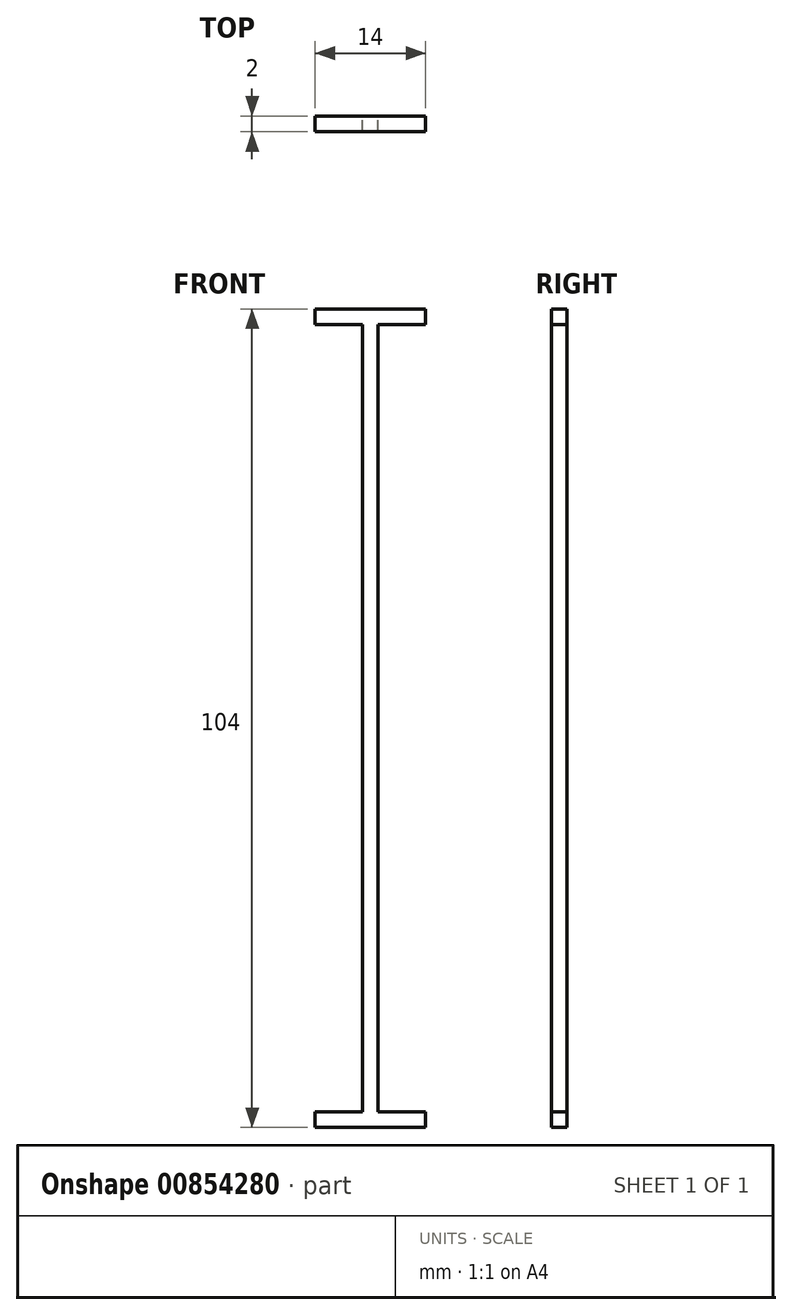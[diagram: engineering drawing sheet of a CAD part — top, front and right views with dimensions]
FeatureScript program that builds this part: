
annotation { "Feature Type Name" : "Feature", "Feature Type Description" : "" }
export const myFeature = defineFeature(function(context is Context, id is Id, definition is map)
    precondition{}
    {
        {
            var Q0;
            Q0=qCreatedBy(makeId("Front.planeOp"),FACE);
            var sketch = newSketch(context, id + "F0", { "sketchPlane" : qUnion([Q0])});
            skLineSegment(sketch, "E0", {"start": v(0, 102) * mm, "end": v(-7, 102) * mm});
            skLineSegment(sketch, "E1", {"start": v(-7, 102) * mm, "end": v(-7, 100) * mm});
            skLineSegment(sketch, "E2", {"start": v(-7, 100) * mm, "end": v(-1, 100) * mm});
            skLineSegment(sketch, "E3", {"start": v(-1, 100) * mm, "end": v(-1, 0) * mm});
            skLineSegment(sketch, "E4", {"start": v(-1, 0) * mm, "end": v(-7, 0) * mm});
            skLineSegment(sketch, "E5", {"start": v(-7, 0) * mm, "end": v(-7, -2) * mm});
            skLineSegment(sketch, "E6", {"start": v(-7, -2) * mm, "end": v(0, -2) * mm});
            skLineSegment(sketch, "E7.MirrorCS", {"start": v(7, 102) * mm, "end": v(7, 100) * mm});
            skLineSegment(sketch, "E8.MirrorCS", {"start": v(7, 0) * mm, "end": v(7, -2) * mm});
            skLineSegment(sketch, "E9.MirrorCS", {"start": v(1, 100) * mm, "end": v(1, 0) * mm});
            skLineSegment(sketch, "E10.MirrorCS", {"start": v(7, 100) * mm, "end": v(1, 100) * mm});
            skLineSegment(sketch, "E11.MirrorCS", {"start": v(7, -2) * mm, "end": v(0, -2) * mm});
            skLineSegment(sketch, "E12.MirrorCS", {"start": v(0, 102) * mm, "end": v(7, 102) * mm});
            skLineSegment(sketch, "E13.MirrorCS", {"start": v(1, 0) * mm, "end": v(7, 0) * mm});
            skSolve(sketch);
        }
        {
            var Q0;
            Q0 = qSketchRegion(id + "F0", true);
            extrude(context, id + "F1", {"entities" : qUnion([Q0]), "depth" : 2 * mm, "offsetDistance" : 25 * mm});
        }
    });
